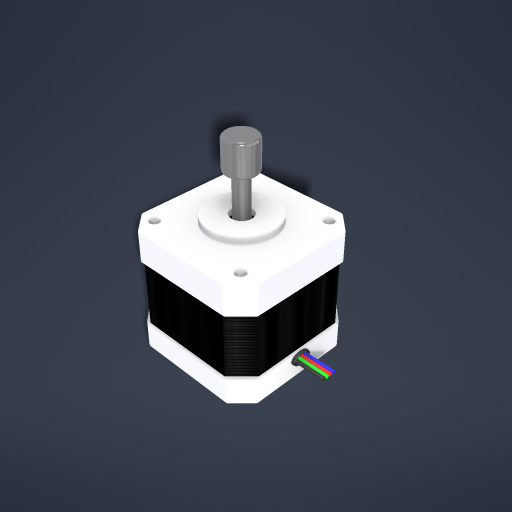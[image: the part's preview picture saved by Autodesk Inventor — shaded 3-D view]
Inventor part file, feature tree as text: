
AUTODESK INVENTOR PART (.ipt)
format: ipt  version: 2023 (Build 270158000, 158)  size: 997,888 bytes
history: native  units: mm
features: extrude x14, sketch x5, fillet x5, hole x4, chamfer x2, plane x1, pattern_linear x1, projected_geometry x1
ambient origin geometry x8: Origin, YZ Plane, XZ Plane, XY Plane, X Axis, Y Axis, Z Axis, Center Point
bodies: Solid1 (feature_tree)
feature tree (33):
  sketch  "Sketch1"  dims[d0=7.0mm d1=22.0mm]
  extrude  "Extrusion1"  Depth=22.0mm
  extrude  "Extrusion2"  Depth=5.0mm
  extrude  "Extrusion3"  Depth=3.0mm
  plane  "Work Plane2"
  extrude  "Extrusion7"  Depth=3.0mm
  extrude  "Extrusion8"  Depth=1.0mm
  chamfer  "Chamfer1"  Distance=42.0mm
  pattern_linear  "Rectangular Pattern2"  Spacing1=135.0deg  [1 undecoded]
  hole  "Hole1"  [1 undecoded]
  hole  "Hole2"  [1 undecoded]
  hole  "Hole3"  [1 undecoded]
  hole  "Hole4"  [1 undecoded]
  extrude  "Extrusion9"  Depth=24.0mm TaperAngle=0.0deg
  fillet  "Fillet1"  Radius=2.0mm
  fillet  "Fillet2"  Radius=39.0mm
  chamfer  "Chamfer2"  [1 undecoded]
  fillet  "Fillet3"  Radius=20.0mm
  sketch  "Sketch6"  dims[d10=3.0mm d11=3.0mm]
  extrude  "Extrusion10"  Depth=1.0mm
  fillet  "Fillet4"  Radius=1.0mm
  extrude  "Extrusion11"  Depth=1.0mm
  extrude  "Extrusion12"  Depth=1.0mm
  extrude  "Extrusion13"  Depth=1.0mm
  extrude  "Extrusion14"  Depth=1.0mm
  extrude  "Extrusion15"  Depth=1.0mm
  sketch  "Sketch11"  dims[d12=3.0mm d39=42.0mm d40=42.0mm d41=135.0deg d42=51.618795mm d43=51.618795mm d44=25.809398mm d45=25.809398mm d46=24.0mm d47=0.0mm d48=2.0mm d49=0.0mm d50=39.0mm d51=0.0mm d60=-10.0mm d126=20.0mm d127=0.0mm d128=1.0mm d129=1.0mm d130=1.0mm d131=1.0mm d132=0.5mm d134=0.5mm d135=0.5mm d136=0.5mm d137=0.5mm d138=1.0mm d139=1.0mm d140=0.5mm d141=0.0mm d145=0.125mm d146=2.0mm d147=45.0deg d148=560.0mm d150=0.5mm d151=10.0mm d152=10.0mm d153=6.0mm d154=6.0mm d155=4.0mm d156=2.0mm d157=90.0deg d158=3.0mm d159=0.0mm d160=10.0mm d161=10.0mm d162=6.0mm d163=6.0mm d164=4.0mm d165=2.0mm d166=90.0deg d167=3.0mm d168=0.0mm d169=10.0mm d170=10.0mm d171=6.0mm d172=6.0mm d173=4.0mm d174=2.0mm d175=90.0deg d176=3.0mm d177=0.0mm d178=10.0mm d179=10.0mm d180=6.0mm d181=6.0mm d182=4.0mm d183=2.0mm d184=90.0deg d185=3.0mm d186=0.0mm d187=41.0mm d188=0.0mm d189=40.0mm d190=0.0mm d191=1.0mm d192=1.0mm d193=0.5mm d194=2.0mm d195=45.0deg d196=0.5mm d197=1.2mm d198=40.0mm d200=1.2mm d201=10.0mm d203=10.0mm d205=2.5mm d206=2.5mm d207=1.0mm d208=0.0mm d209=0.3mm d210=10.0mm d211=0.0mm d212=10.0mm d213=0.0mm d214=10.0mm d215=0.0mm d216=10.0mm d217=0.0mm d218=0.2mm d219=5.0mm d220=0.0mm d221=0.0mm d225=10.0mm d226=10.0mm d227=0.0mm d228=10.0mm d229=0.0mm d230=1.0mm]
  extrude  "Extrusion16"  Depth=1.0mm
  extrude  "Extrusion17"  Depth=1.0mm
  fillet  "Fillet5"  Radius=0.5mm
  sketch  "Sketch4"  dims[d4=5.0mm d5=31.0mm]
  projected_geometry  "Projected Loop2"
  sketch  "Sketch5"  dims[d6=31.0mm d9=3.0mm]
note: 6 required parameter values undecoded (feature->parameter linkage not recoverable at this tier; creation-order binding heuristic only, values carry confidence <= 0.55)
